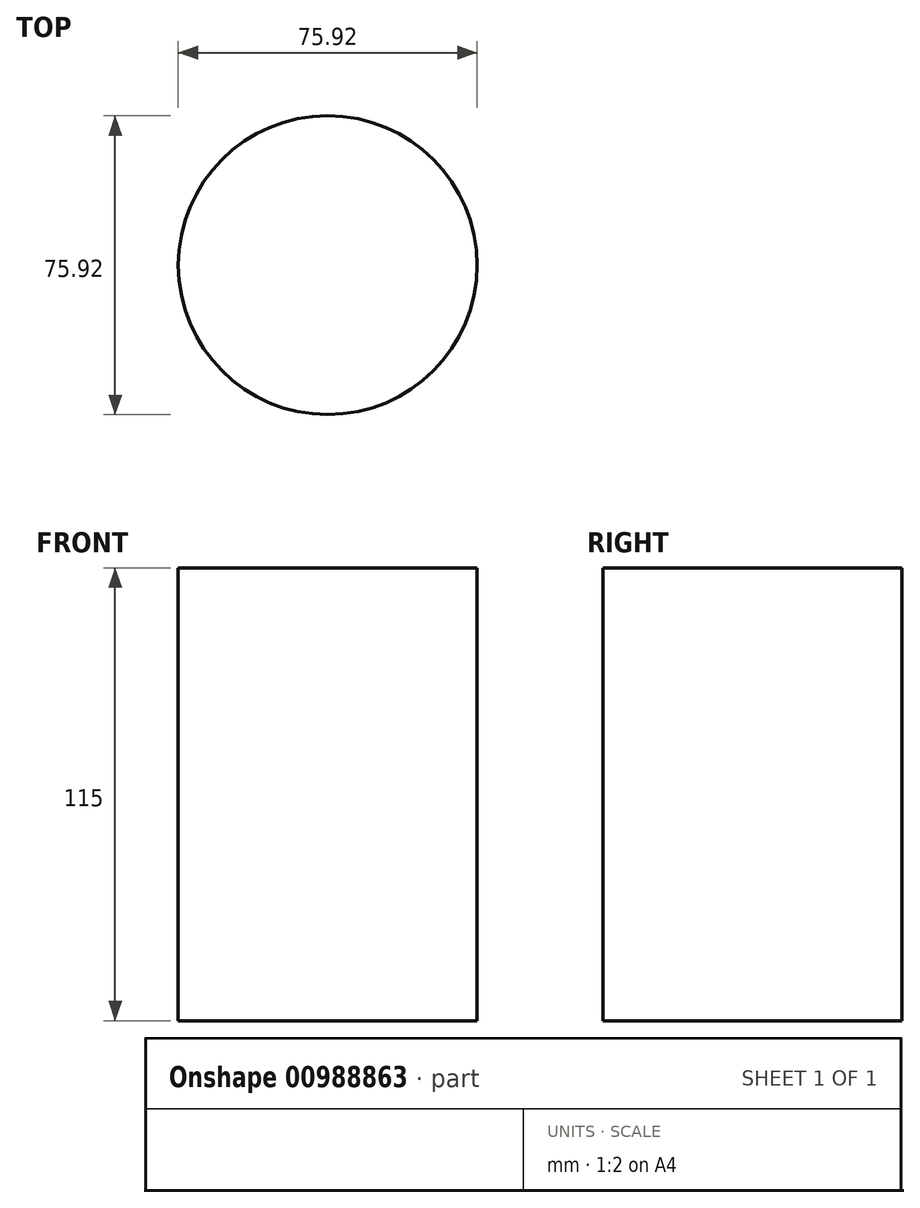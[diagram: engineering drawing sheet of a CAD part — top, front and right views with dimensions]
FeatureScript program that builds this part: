
annotation { "Feature Type Name" : "Feature", "Feature Type Description" : "" }
export const myFeature = defineFeature(function(context is Context, id is Id, definition is map)
    precondition{}
    {
        {
            var Q0;
            Q0=qCreatedBy(makeId("Top.planeOp"),FACE);
            var sketch = newSketch(context, id + "F0", { "sketchPlane" : qUnion([Q0])});
            skCircle(sketch, "E0", {"center": v(0, 0) * mm, "radius": 37.96 * mm});
            skSolve(sketch);
        }
        {
            var Q0;
            Q0 = qSketchRegion(id + "F0", true);
            extrude(context, id + "F1", {"entities" : qUnion([Q0]), "depth" : 115 * mm, "offsetDistance" : 25 * mm});
        }
    });
